# Revit family: CIRCLE STAIR LIGHT_CM1W.1
name_source: partatom
category: Luminarias
units: mm (PartAtom-declared; Revit-internal decimal feet)

## family parameters
Compartido = No
Corte con vacíos al cargar = No
Cota de conector redondo = Diámetro de uso
Origen de luz = Sí
Punto de cálculo de habitación = No
Se basa en plano de trabajo = Sí
Siempre vertical = No
Tipo de pieza = Normal

## types (1)
- CIRCLE STAIR LIGHT_CM1W.1
    Archivo de red fotométrica = CM1W.1_3000K _20°.IES
    Cambio de temperatura de color de luz atenuada = <Ninguno>
    Comentarios de vataje = 24V
    Descripción = LUMINARIA TIPO CIRCULAR PARA EMPOTRAR EN MURO CON CUERPO DE ALUMINIO FUNDIDO A PRESION CUBIERTO CON POLVO GRIS OSCURO, IP 67 USO PARA INTERIORES O EXTERIORES CON CUERPO DE 0.2KG, CUENTA CON 1 LED OSRAM CON UNA POTENCIA TOTAL DE 1.3W, A UNA TEMPERATURA EN BLANCO CALIDO 3000K CON 23 LUMENES, EFICIENCIA DE 17.69LM/W, IRC 80, IK10, APERTURA A 20 GRADOS POR PROYECTO, 54mA EN CORRIENTE DE OPERACIÓN, ALIMENTADA A 24V. REQUIERE ACCESORIOS.
    Elevación por defecto = 0 mm  [stored 0 ft]
    Fabricante = BRILLANT
    Filtro de color = 16777215
    Lámpara = OSRAM
    Modelo = CM1W.1
    Watt per fixture = 1.3
    Ángulo de inclinación = 60.00°

note: [stored X ft] marks values corroborated as IEEE doubles in the binary element streams (Revit-internal decimal feet)

## geometry (parser evidence)
native form markers: Blend x2
no freeform markers — native parametric forms only
